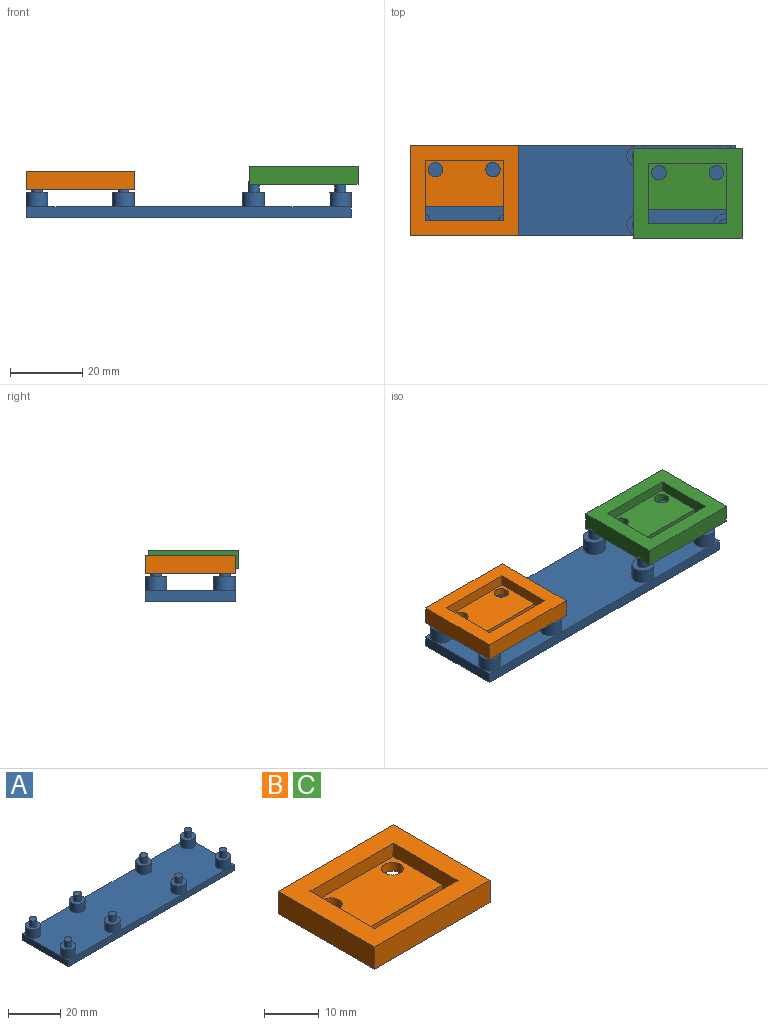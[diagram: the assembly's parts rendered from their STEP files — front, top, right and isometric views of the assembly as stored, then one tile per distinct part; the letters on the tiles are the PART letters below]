
ASSEMBLY  parts=3 mates=1
PART A: 42 faces, bbox 90x25x10 mm
  f0: plane 90x25mm, normal (0,0,1), area 2016.1mm2, adj f4,f5,f6,f7,f10,f12,f14,f16
  f1: plane 3x3mm, normal (0,0,1), area 1.9mm2, adj f6,f7,f22
  f2: plane 3x3mm, normal (0,0,1), area 1.9mm2, adj f4,f5,f16
  f3: plane 3x3mm, normal (0,0,1), area 1.9mm2, adj f4,f7,f10
  f4: plane 25x3mm, normal (-1,0,0), area 75mm2, adj f0,f2,f3,f5,f7,f9
  f5: plane 90x3mm, normal (0,-1,0), area 270mm2, adj f0,f2,f4,f6,f8,f9
  f6: plane 25x3mm, normal (1,0,0), area 75mm2, adj f0,f1,f5,f7,f8,f9
  f7: plane 90x3mm, normal (0,1,0), area 270mm2, adj f0,f1,f3,f4,f6,f9
  f8: plane 3x3mm, normal (0,0,1), area 1.9mm2, adj f5,f6,f24
  f9: plane 90x25mm, normal (0,0,-1), area 2250mm2, adj f4,f5,f6,f7
  f10: cylinder r=3mm len=6mm, axis (0,0,-1), area 75.4mm2, adj f0,f3,f11
  f11: plane 6x6mm, normal (0,0,1), area 21.2mm2, adj f10,f26
  f12: cylinder r=3mm len=6mm, axis (0,0,-1), area 75.4mm2, adj f0,f13
  f13: plane 6x6mm, normal (0,0,1), area 21.2mm2, adj f12,f30
  f14: cylinder r=3mm len=6mm, axis (0,0,-1), area 75.4mm2, adj f0,f15
  f15: plane 6x6mm, normal (0,0,1), area 21.2mm2, adj f14,f32
  f16: cylinder r=3mm len=6mm, axis (0,0,-1), area 75.4mm2, adj f0,f2,f17
  f17: plane 6x6mm, normal (0,0,1), area 21.2mm2, adj f16,f28
  f18: cylinder r=3mm len=6mm, axis (0,0,-1), area 75.4mm2, adj f0,f19
  f19: plane 6x6mm, normal (0,0,1), area 21.2mm2, adj f18,f34
  f20: cylinder r=3mm len=6mm, axis (0,0,-1), area 75.4mm2, adj f0,f21
  f21: plane 6x6mm, normal (0,0,1), area 21.2mm2, adj f20,f36
  f22: cylinder r=3mm len=6mm, axis (0,0,-1), area 75.4mm2, adj f0,f1,f23
  f23: plane 6x6mm, normal (0,0,1), area 21.2mm2, adj f22,f38
  f24: cylinder r=3mm len=6mm, axis (0,0,-1), area 75.4mm2, adj f0,f8,f25
  f25: plane 6x6mm, normal (0,0,1), area 21.2mm2, adj f24,f40
  f26: cylinder r=1.5mm len=3mm, axis (0,0,-1), area 28.3mm2, adj f11,f27
  f27: plane 3x3mm, normal (0,0,1), area 7.1mm2, adj f26
  f28: cylinder r=1.5mm len=3mm, axis (0,0,-1), area 28.3mm2, adj f17,f29
  f29: plane 3x3mm, normal (0,0,1), area 7.1mm2, adj f28
  f30: cylinder r=1.5mm len=3mm, axis (0,0,-1), area 28.3mm2, adj f13,f31
  f31: plane 3x3mm, normal (0,0,1), area 7.1mm2, adj f30
  f32: cylinder r=1.5mm len=3mm, axis (0,0,-1), area 28.3mm2, adj f15,f33
  f33: plane 3x3mm, normal (0,0,1), area 7.1mm2, adj f32
  f34: cylinder r=1.5mm len=3mm, axis (0,0,-1), area 28.3mm2, adj f19,f35
  f35: plane 3x3mm, normal (0,0,1), area 7.1mm2, adj f34
  f36: cylinder r=1.5mm len=3mm, axis (0,0,-1), area 28.3mm2, adj f21,f37
  f37: plane 3x3mm, normal (0,0,1), area 7.1mm2, adj f36
  f38: cylinder r=1.5mm len=3mm, axis (0,0,-1), area 28.3mm2, adj f23,f39
  f39: plane 3x3mm, normal (0,0,1), area 7.1mm2, adj f38
  f40: cylinder r=1.5mm len=3mm, axis (0,0,-1), area 28.3mm2, adj f25,f41
  f41: plane 3x3mm, normal (0,0,1), area 7.1mm2, adj f40
PART B: 22 faces, bbox 30x25x5 mm
  f0: plane 30x25mm, normal (0,0,-1), area 600mm2, adj f1,f2,f4,f5,f6,f7,f8,f11
  f1: plane 21.6x5mm, normal (0,1,0), area 107mm2, adj f0,f2,f4,f9,f18,f19,f20,f21
  f2: plane 16.8x5mm, normal (1,0,0), area 57.7mm2, adj f0,f1,f3,f9,f10,f11,f16,f17
  f3: plane 21.6x3mm, normal (0,-1,0), area 64.5mm2, adj f2,f4,f9,f10,f14,f15,f16,f17
  f4: plane 16.8x5mm, normal (-1,0,0), area 57.7mm2, adj f0,f1,f3,f9,f10,f11,f14,f15
  f5: plane 25x5mm, normal (-1,0,0), area 125mm2, adj f0,f6,f8,f9
  f6: plane 30x5mm, normal (0,-1,0), area 150mm2, adj f0,f5,f7,f9
  f7: plane 25x5mm, normal (1,0,0), area 125mm2, adj f0,f6,f8,f9
  f8: plane 30x5mm, normal (0,1,0), area 150mm2, adj f0,f5,f7,f9
  f9: plane 30x25mm, normal (0,0,1), area 387.1mm2, adj f1,f2,f3,f4,f5,f6,f7,f8
  f10: plane 21.6x12.8mm, normal (0,0,1), area 251.3mm2, adj f2,f3,f4,f11,f12,f13,f15,f16
  f11: plane 21.6x2mm, normal (0,-1,0), area 43.2mm2, adj f0,f2,f4,f10
  f12: cylinder r=2mm len=4mm, axis (0,0,1), area 25.1mm2, adj f0,f10
  f13: cylinder r=2mm len=4mm, axis (0,0,1), area 25.1mm2, adj f0,f10
  f14: plane 3.5x3.5mm, normal (0,0,-1), area 9.6mm2, adj f3,f4,f15
  f15: cylinder r=1.75mm len=3.5mm, axis (0,0,-1), area 32.7mm2, adj f0,f3,f4,f10,f14
  f16: cylinder r=1.75mm len=3.5mm, axis (0,0,-1), area 32.7mm2, adj f0,f2,f3,f10,f17
  f17: plane 3.5x3.5mm, normal (0,0,-1), area 9.6mm2, adj f2,f3,f16
  f18: cylinder r=1.75mm len=3.5mm, axis (0,0,-1), area 32.3mm2, adj f0,f1,f4,f19
  f19: plane 3.5x3.5mm, normal (0,0,-1), area 9.6mm2, adj f1,f4,f18
  f20: cylinder r=1.75mm len=3.5mm, axis (0,0,-1), area 32.3mm2, adj f0,f1,f2,f21
  f21: plane 3.5x3.5mm, normal (0,0,-1), area 9.6mm2, adj f1,f2,f20
PART C: same geometry as B
PLACE A t=(25.15,65.83,-18.68)mm
PLACE B t=(-23.84,15.84,-10.91)mm
PLACE C t=(38.03,14.98,-9.46)mm
MATE cylindrical B.f18 <-> A.f14  axis (0,0,-1) through (-11.84,6.34,-10.91)mm
